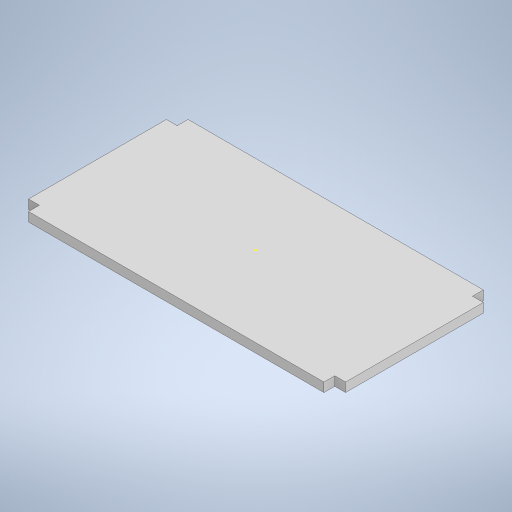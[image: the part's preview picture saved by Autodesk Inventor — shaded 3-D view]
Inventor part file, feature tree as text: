
AUTODESK INVENTOR PART (.ipt)
format: ipt  version: 2023 (Build 270158000, 158)  size: 238,592 bytes
history: native  units: in
note: dims shown in document units (in); Inventor stores cm internally (conversion verified against a paired STEP export)
features: sketch x4, extrude x2, mirror x2
ambient origin geometry x8: Origin, YZ Plane, XZ Plane, XY Plane, X Axis, Y Axis, Z Axis, Center Point
bodies: Solid1 (feature_tree)
feature tree (8):
  extrude  "Extrusion1"  Depth=15.3071in
  sketch  "Sketch2"  dims[d2=0.875in d3=0.0in]
  sketch  "Sketch3"  dims[d4=0.0394in]
  extrude  "Extrusion2"  TaperAngle=0.0deg  [1 undecoded]
  mirror  "Mirror1"
  mirror  "Mirror2"
  sketch  "Sketch1"  dims[d0=30.4252in d1=15.3071in]
  sketch  "Sketch4"  dims[d5=0.0394in d6=1.0394in d7=0.875in d8=0.0in]
note: 1 required parameter value undecoded (feature->parameter linkage not recoverable at this tier; creation-order binding heuristic only, values carry confidence <= 0.55)
